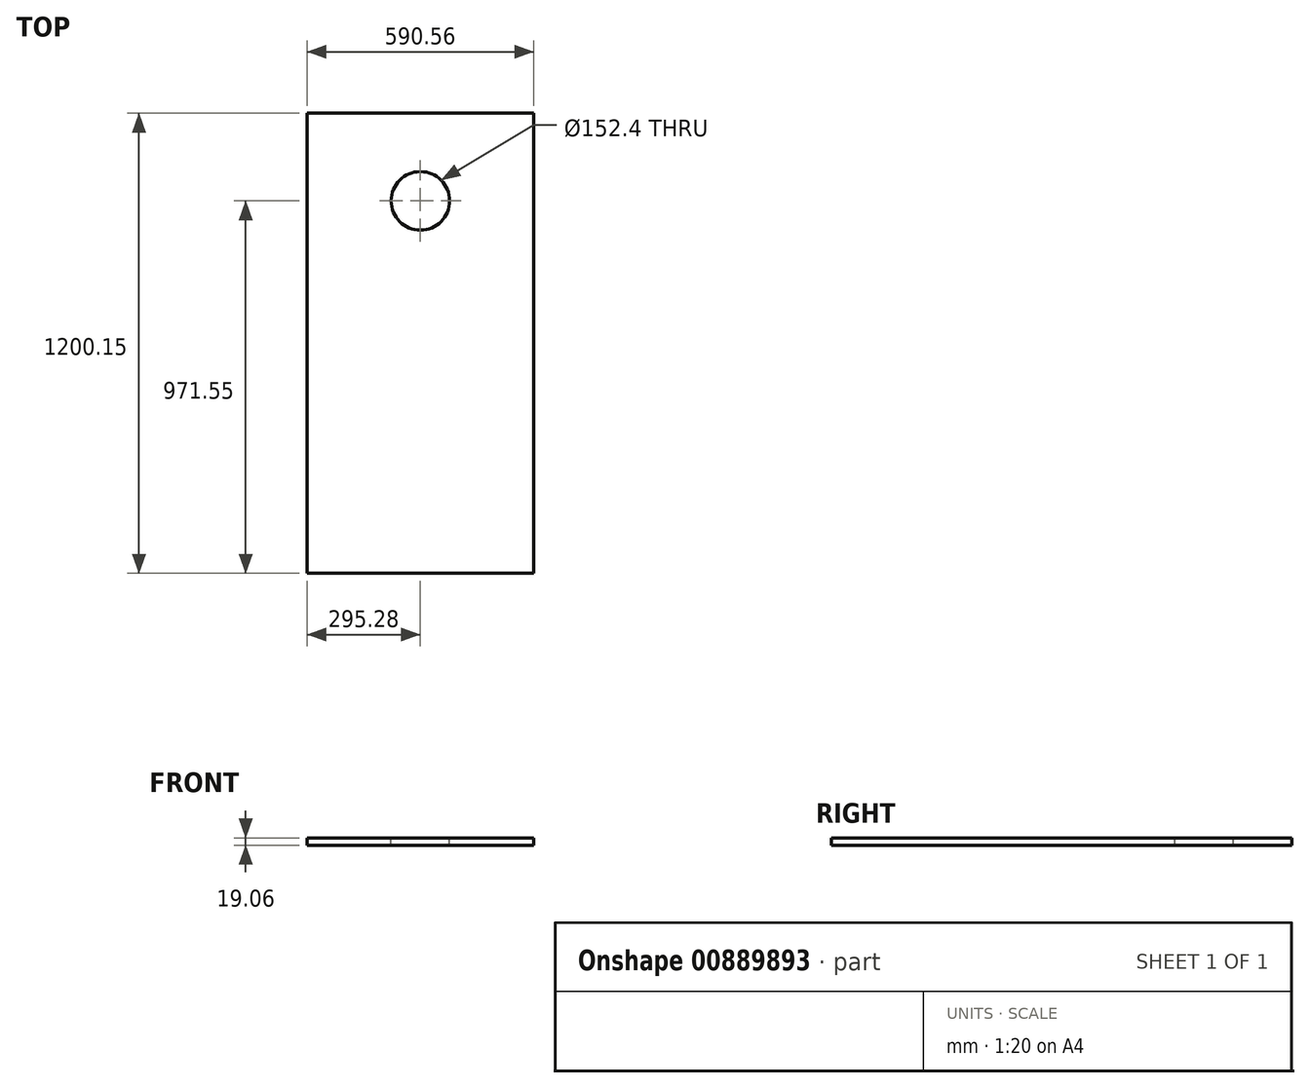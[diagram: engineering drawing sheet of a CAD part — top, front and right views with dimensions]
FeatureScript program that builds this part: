
annotation { "Feature Type Name" : "Feature", "Feature Type Description" : "" }
export const myFeature = defineFeature(function(context is Context, id is Id, definition is map)
    precondition{}
    {
        {
            var Q0;
            Q0=qCreatedBy(makeId("Front.planeOp"),FACE);
            var sketch = newSketch(context, id + "F0", { "sketchPlane" : qUnion([Q0])});
            skLineSegment(sketch, "E0.bottom", {"start": v(295.27, -9.53) * mm, "end": v(-295.27, -9.53) * mm});
            skLineSegment(sketch, "E0.top", {"start": v(295.28, 9.53) * mm, "end": v(-295.27, 9.53) * mm});
            skLineSegment(sketch, "E0.left", {"start": v(295.28, -9.53) * mm, "end": v(295.28, 9.52) * mm});
            skLineSegment(sketch, "E0.right", {"start": v(-295.27, -9.53) * mm, "end": v(-295.27, 9.52) * mm});
            skPoint(sketch, "E0.middle", {"position": v(0, 0) * mm});
            skSolve(sketch);
        }
        {
            var Q0;
            Q0 = qSketchRegion(id + "F0", true);
            extrude(context, id + "F1", {"entities" : qUnion([Q0]), "depth" : 1200.15 * mm, "offsetDistance" : 25.4 * mm});
        }
        {
            var Q0;
            Q0=makeQuery(id+"F1.opExtrude","SWEPT_FACE",FACE,{"disambiguationData":[OSD([sQuery(id+"F0.wireOp",EDGE,"E0.top")])]});
            var sketch = newSketch(context, id + "F2", { "sketchPlane" : qUnion([Q0])});
            skLineSegment(sketch, "E1", {"start": v(0, 0) * mm, "end": v(0, -228.6) * mm, "construction": true});
            skLineSegment(sketch, "E2", {"start": v(0, -228.6) * mm, "end": v(295.28, -228.6) * mm, "construction": true});
            skSolve(sketch);
        }
        {
            var Q0;
            Q0=sQuery(id+"F2.wireOp",VERTEX,"E1.end");
            var Q1;
            Q1=makeQuery(id+"F1.opExtrude","SWEPT_BODY",BODY,{"disambiguationData":[OSD([sQuery(id+"F0.wireOp",EDGE,"E0.bottom"),sQuery(id+"F0.wireOp",EDGE,"E0.top"),sQuery(id+"F0.wireOp",EDGE,"E0.left"),sQuery(id+"F0.wireOp",EDGE,"E0.right")])]});
            hole(context, id + "F3", {"style" : HoleStyle.SIMPLE, "endStyle" : HoleEndStyle.THROUGH, "holeDiameter" : 152.4 * mm, "majorDiameter" : 6.35 * mm, "isTappedThrough" : true, "tappedDepth" : 12.7 * mm, "tapClearance" : 3, "locations" : qUnion([Q0]), "scope" : qUnion([Q1])});
        }
    });
